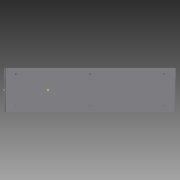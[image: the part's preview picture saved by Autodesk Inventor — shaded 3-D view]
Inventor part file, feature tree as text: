
AUTODESK INVENTOR PART (.ipt)
format: ipt  version: 2015 (Build 190159000, 159)  size: 185,344 bytes
history: native  units: mm
features: other x6, hole x6, sheet_metal_op x4, chamfer x4, sketch x4, mirror x1
ambient origin geometry x8: Origin, YZ Plane, XZ Plane, XY Plane, X Axis, Y Axis, Z Axis, Center Point
bodies: Solid1 (feature_tree)
feature tree (25):
  sheet_metal_op  "Face1"
  sheet_metal_op  "Flange1"
  other  "A-Side Definition"
  other  "Corner Chamfer1"
  chamfer  "Corner Round1"
  chamfer  "Corner Round2"
  mirror  "Mirror1"
  other  "Corner Chamfer2"
  chamfer  "Corner Round3"
  chamfer  "Corner Round5"
  hole  "Hole1"  [1 undecoded]
  hole  "Hole2"  [1 undecoded]
  hole  "Hole3"  [1 undecoded]
  hole  "Hole4"  [1 undecoded]
  hole  "Hole5"  [1 undecoded]
  hole  "Hole6"  [1 undecoded]
  sketch  "Sketch3"  dims[d4=0.75mm d5=3.0mm]
  sketch  "Sketch4"  dims[d6=1.5mm d7=35.0mm d8=90.0deg d9=1.5mm d10=6.0mm d11=1.5mm d12=1.5mm d13=10.0mm d14=58.5mm d15=45.0deg d16=0.25mm d17=0.25mm d18=58.5mm d19=10.0mm d20=45.0deg d21=0.25mm d23=0.25mm d24=17.0mm d25=10.5mm d26=3.2mm d27=6.0mm d28=4.0mm d29=2.0mm d30=90.0deg d31=1.5mm d32=20.594885mm d33=10.5mm d34=17.0mm d35=3.2mm d36=6.0mm d37=4.0mm d38=2.0mm d39=90.0deg d40=1.5mm d41=20.594885mm d42=17.0mm d43=10.5mm d44=3.2mm d45=6.0mm d46=4.0mm d47=2.0mm d48=90.0deg d49=1.5mm d50=20.594885mm d51=17.0mm d52=10.5mm d53=3.2mm d54=6.0mm d55=4.0mm d56=2.0mm d57=90.0deg d58=1.5mm d59=20.594885mm d60=10.5mm d61=147.0mm d62=3.2mm d63=6.0mm d64=4.0mm d65=2.0mm d66=90.0deg d67=1.5mm d68=20.594885mm d69=10.5mm d70=147.0mm d71=3.2mm d72=6.0mm d73=4.0mm d74=2.0mm d75=90.0deg d76=1.5mm d77=20.594885mm]
  sketch  "Sketch1"  dims[d0=77.0mm d1=147.0mm]
  other  "Plate1"
  sketch  "Sketch2"  dims[d2=1.5mm d3=1.5mm]
  other  "Plate2"
  sheet_metal_op  "Bend1"
  sheet_metal_op  "Corner1"
  other  "Definition1"
note: 6 required parameter values undecoded (feature->parameter linkage not recoverable at this tier; creation-order binding heuristic only, values carry confidence <= 0.55)
